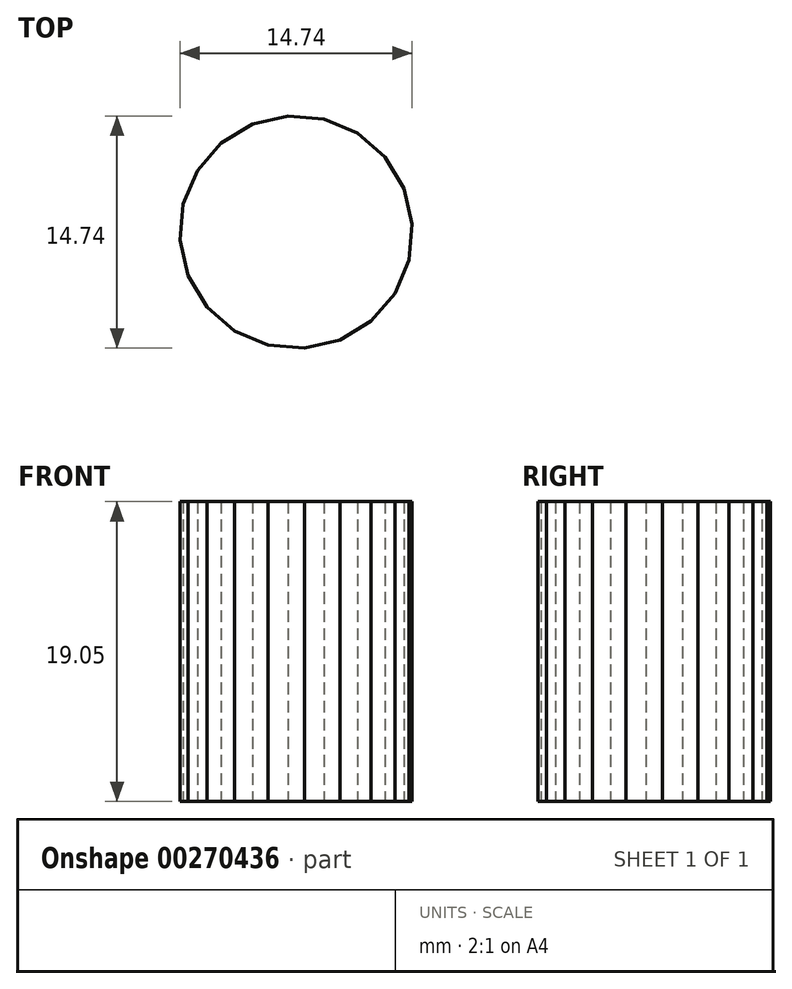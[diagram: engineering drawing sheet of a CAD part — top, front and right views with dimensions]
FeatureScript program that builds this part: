
annotation { "Feature Type Name" : "Feature", "Feature Type Description" : "" }
export const myFeature = defineFeature(function(context is Context, id is Id, definition is map)
    precondition{}
    {
        {
            var Q0;
            Q0=qCreatedBy(makeId("Top.planeOp"),FACE);
            var sketch = newSketch(context, id + "F0", { "sketchPlane" : qUnion([Q0])});
            skCircle(sketch, "E0.cCircle", {"center": v(0, 0) * mm, "radius": 7.3 * mm, "construction": true});
            skLineSegment(sketch, "E0.0", {"start": v(3.91, 6.27) * mm, "end": v(5.66, 4.76) * mm});
            skLineSegment(sketch, "E0.1", {"start": v(5.66, 4.76) * mm, "end": v(6.85, 2.77) * mm});
            skLineSegment(sketch, "E0.2", {"start": v(6.85, 2.77) * mm, "end": v(7.37, 0.52) * mm});
            skLineSegment(sketch, "E0.3", {"start": v(7.37, 0.52) * mm, "end": v(7.17, -1.78) * mm});
            skLineSegment(sketch, "E0.4", {"start": v(7.17, -1.78) * mm, "end": v(6.27, -3.91) * mm});
            skLineSegment(sketch, "E0.5", {"start": v(6.27, -3.91) * mm, "end": v(4.76, -5.66) * mm});
            skLineSegment(sketch, "E0.6", {"start": v(4.76, -5.66) * mm, "end": v(2.77, -6.85) * mm});
            skLineSegment(sketch, "E0.7", {"start": v(2.77, -6.85) * mm, "end": v(0.52, -7.37) * mm});
            skLineSegment(sketch, "E0.8", {"start": v(0.52, -7.37) * mm, "end": v(-1.78, -7.17) * mm});
            skLineSegment(sketch, "E0.9", {"start": v(-1.78, -7.17) * mm, "end": v(-3.91, -6.27) * mm});
            skLineSegment(sketch, "E0.10", {"start": v(-3.91, -6.27) * mm, "end": v(-5.66, -4.76) * mm});
            skLineSegment(sketch, "E0.11", {"start": v(-5.66, -4.76) * mm, "end": v(-6.85, -2.77) * mm});
            skLineSegment(sketch, "E0.12", {"start": v(-6.85, -2.77) * mm, "end": v(-7.37, -0.52) * mm});
            skLineSegment(sketch, "E0.13", {"start": v(-7.37, -0.52) * mm, "end": v(-7.17, 1.78) * mm});
            skLineSegment(sketch, "E0.14", {"start": v(-7.17, 1.78) * mm, "end": v(-6.27, 3.91) * mm});
            skLineSegment(sketch, "E0.15", {"start": v(-6.27, 3.91) * mm, "end": v(-4.76, 5.66) * mm});
            skLineSegment(sketch, "E0.16", {"start": v(-4.76, 5.66) * mm, "end": v(-2.77, 6.85) * mm});
            skLineSegment(sketch, "E0.17", {"start": v(-2.77, 6.85) * mm, "end": v(-0.52, 7.37) * mm});
            skLineSegment(sketch, "E0.18", {"start": v(-0.52, 7.37) * mm, "end": v(1.78, 7.17) * mm});
            skLineSegment(sketch, "E0.19", {"start": v(1.78, 7.17) * mm, "end": v(3.91, 6.27) * mm});
            skPoint(sketch, "E0.0.midPoint", {"position": v(4.79, 5.51) * mm});
            skSolve(sketch);
        }
        {
            var Q0;
            Q0 = qSketchRegion(id + "F0", true);
            extrude(context, id + "F1", {"entities" : qUnion([Q0]), "depth" : 19.05 * mm});
        }
    });
